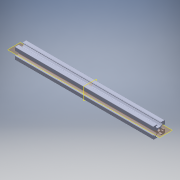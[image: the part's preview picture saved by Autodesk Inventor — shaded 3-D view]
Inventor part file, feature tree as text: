
AUTODESK INVENTOR PART (.ipt)
format: ipt  version: 2018 (Build 220112000, 112)  size: 377,856 bytes
history: native  units: in
note: dims shown in document units (in); Inventor stores cm internally (conversion verified against a paired STEP export)
features: extrude x1, plane x1, sketch x1, projected_geometry x1, fillet x1
ambient origin geometry x8: Origin, YZ Plane, XZ Plane, XY Plane, X Axis, Y Axis, Z Axis, Center Point
bodies: Solid1 (feature_tree)
feature tree (5):
  extrude  "Extrusion2"  [1 undecoded]
  plane  "Work Plane1"
  sketch  "Sketch3"  dims[d2=5.5118in d3=0.0in]
  projected_geometry  "Projected Loop2"
  fillet  "Fillet5"  [1 undecoded]
note: 2 required parameter values undecoded (feature->parameter linkage not recoverable at this tier; creation-order binding heuristic only, values carry confidence <= 0.55)
